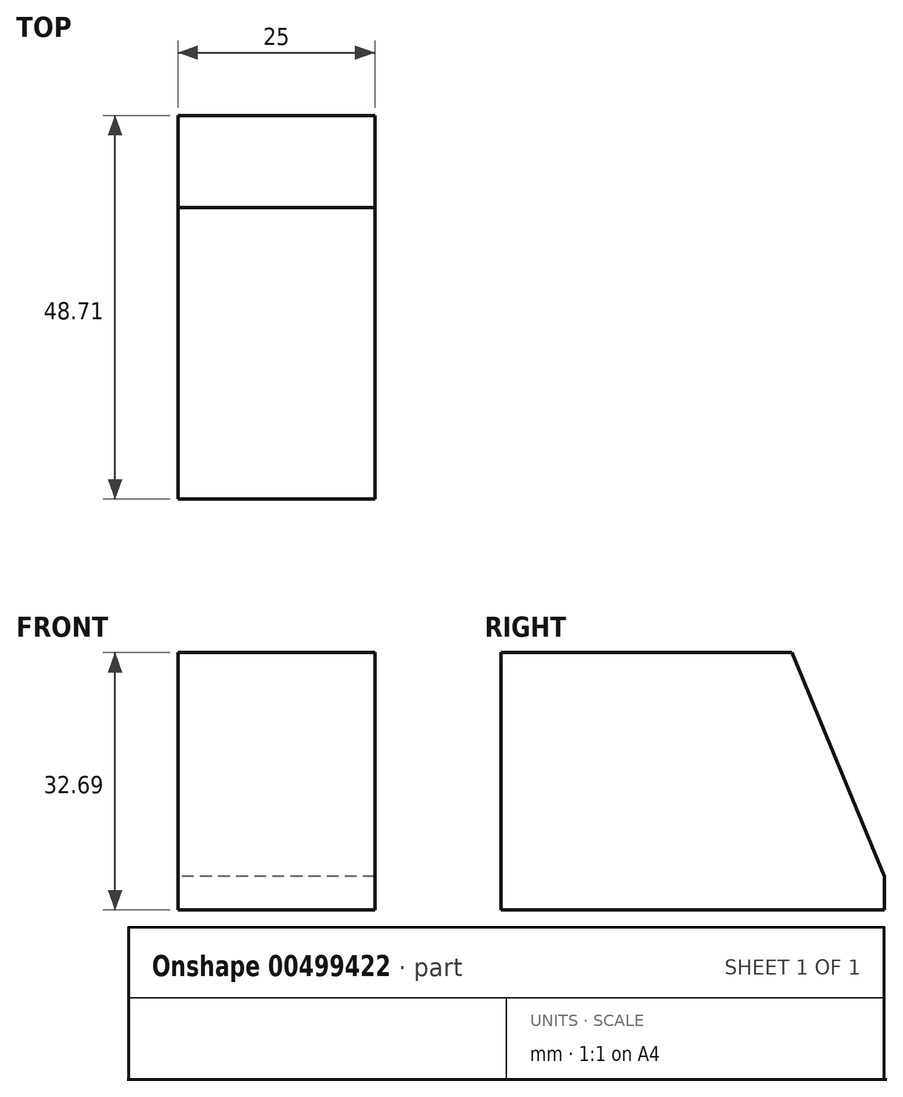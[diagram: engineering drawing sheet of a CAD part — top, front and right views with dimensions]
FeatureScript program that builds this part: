
annotation { "Feature Type Name" : "Feature", "Feature Type Description" : "" }
export const myFeature = defineFeature(function(context is Context, id is Id, definition is map)
    precondition{}
    {
        {
            var Q0;
            Q0=qCreatedBy(makeId("Right.planeOp"),FACE);
            var sketch = newSketch(context, id + "F0", { "sketchPlane" : qUnion([Q0])});
            skLineSegment(sketch, "E0", {"start": v(0, 0) * mm, "end": v(0, 32.7) * mm});
            skLineSegment(sketch, "E1", {"start": v(0, 32.7) * mm, "end": v(37.02, 32.7) * mm});
            skLineSegment(sketch, "E2", {"start": v(37.02, 32.7) * mm, "end": v(48.71, 4.25) * mm});
            skLineSegment(sketch, "E3", {"start": v(48.71, 4.25) * mm, "end": v(48.71, 0) * mm});
            skLineSegment(sketch, "E4", {"start": v(48.71, 0) * mm, "end": v(0, 0) * mm});
            skSolve(sketch);
        }
        {
            var Q0;
            Q0 = qSketchRegion(id + "F0", true);
            extrude(context, id + "F1", {"entities" : qUnion([Q0]), "endBound" : BoundingType.SYMMETRIC, "depth" : 25 * mm});
        }
    });
